# Revit family: Sidewall_Propeller_Fan-Carnes-LNBK-K_Series
name_source: partatom
category: Mechanical Equipment
revit_build: Autodesk Revit MEP 2012 (Build: 20110309_2315(x64)
units: mm (PartAtom-declared; Revit-internal decimal feet)

## types (7) — shared parameters
04 CSI = 23 34 16
95 CSI = 15830
Assembly Code = D3040200
Catalog URL = http://www.carnes.com
Default Elevation = 4' - 0"
Description = K Series SideWall Propellar Fan
Flor Rate = 0 CFM
IOM Instructions URL = http://www.carnes.com
Manufacturer = CARNES COMPANY
Manufacturer Fax = 608-845-6470
Material = Cast Aluminum
Parts List URL = http://www.carnes.com
Product Page URL = http://www.carnes.com
Spec Sheet URL = http://www.carnes.com
Subcategory = Sidewall Propeller Fan
Support Weight Less Motor = 0' - 0"
URL = http://www.carnes.com
Unit = Aluminum-Carnes-Spun-Brushed
ecoScorecard Product Page = http://ecoscorecard.com
zero-valued in all types: Rated CFM

## per-type parameters (varying)
| type | A | BS | CS | D | F Dia | Wgt. less Mtr. |
| LNBK 24 | 2' - 6" | 1' - 10" | 1' - 7 7/8" | 0' - 2 1/8" | 2' - 0 1/2" | 100lbs.-46Kg. |
| LNBK 30 | 3' - 0" | 1' - 10" | 1' - 7 7/8" | 0' - 2 1/8" | 2' - 6 1/2" | 112lbs.-51Kg. |
| LNBK 36 | 3' - 6" | 1' - 10" | 1' - 7 7/8" | 0' - 2 1/8" | 3' - 0 1/2" | 126lbs.-57Kg. |
| LNBK 42 | 4' - 0" | 2' - 2" | 1' - 11 7/8" | 0' - 2 1/8" | 3' - 6 1/2" | 136lbs.-62Kg. |
| LNBK 48 | 4' - 6" | 2' - 5" | 2' - 2 7/8" | 0' - 2 1/8" | 4' - 0 1/2" | 161lbs.-73Kg. |
| LNBK 54 | 5' - 0" | 2' - 8" | 2' - 5 1/4" | 0' - 2 3/4" | 4' - 7 1/2" | 225lbs.-102Kg. |
| LNBK 60 | 5' - 6" | 2' - 10" | 2' - 7 1/4" | 0' - 2 3/4" | 5' - 1 3/4" | 270lbs.-122Kg. |

note: column(s) folded — value = type name in every type: Model

## geometry (parser evidence)
native form markers: Sweep x6
no freeform markers — native parametric forms only
